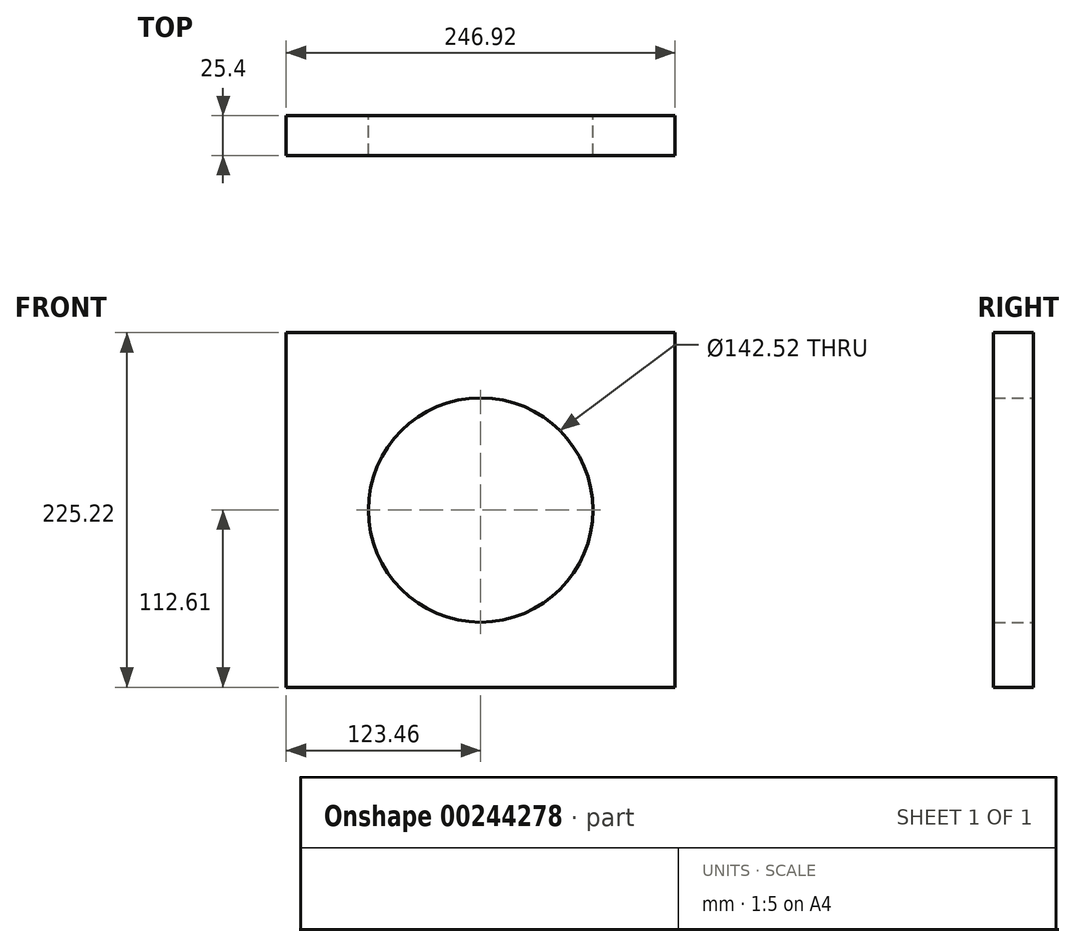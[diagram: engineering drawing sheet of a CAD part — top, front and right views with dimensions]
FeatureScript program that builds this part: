
annotation { "Feature Type Name" : "Feature", "Feature Type Description" : "" }
export const myFeature = defineFeature(function(context is Context, id is Id, definition is map)
    precondition{}
    {
        {
            var Q0;
            Q0=qCreatedBy(makeId("Front.planeOp"),FACE);
            var sketch = newSketch(context, id + "F0", { "sketchPlane" : qUnion([Q0])});
            skLineSegment(sketch, "E0.bottom", {"start": v(-123.46, -112.61) * mm, "end": v(123.46, -112.61) * mm});
            skLineSegment(sketch, "E0.top", {"start": v(-123.46, 112.61) * mm, "end": v(123.46, 112.61) * mm});
            skLineSegment(sketch, "E0.left", {"start": v(-123.46, -112.61) * mm, "end": v(-123.46, 112.61) * mm});
            skLineSegment(sketch, "E0.right", {"start": v(123.46, -112.61) * mm, "end": v(123.46, 112.61) * mm});
            skPoint(sketch, "E0.middle", {"position": v(0, 0) * mm});
            skCircle(sketch, "E1", {"center": v(0, 0) * mm, "radius": 71.26 * mm});
            skSolve(sketch);
        }
        {
            var Q0;
            Q0 = qSketchRegion(id + "F0", true);
            extrude(context, id + "F1", {"entities" : qUnion([Q0]), "depth" : 25.4 * mm});
        }
    });
